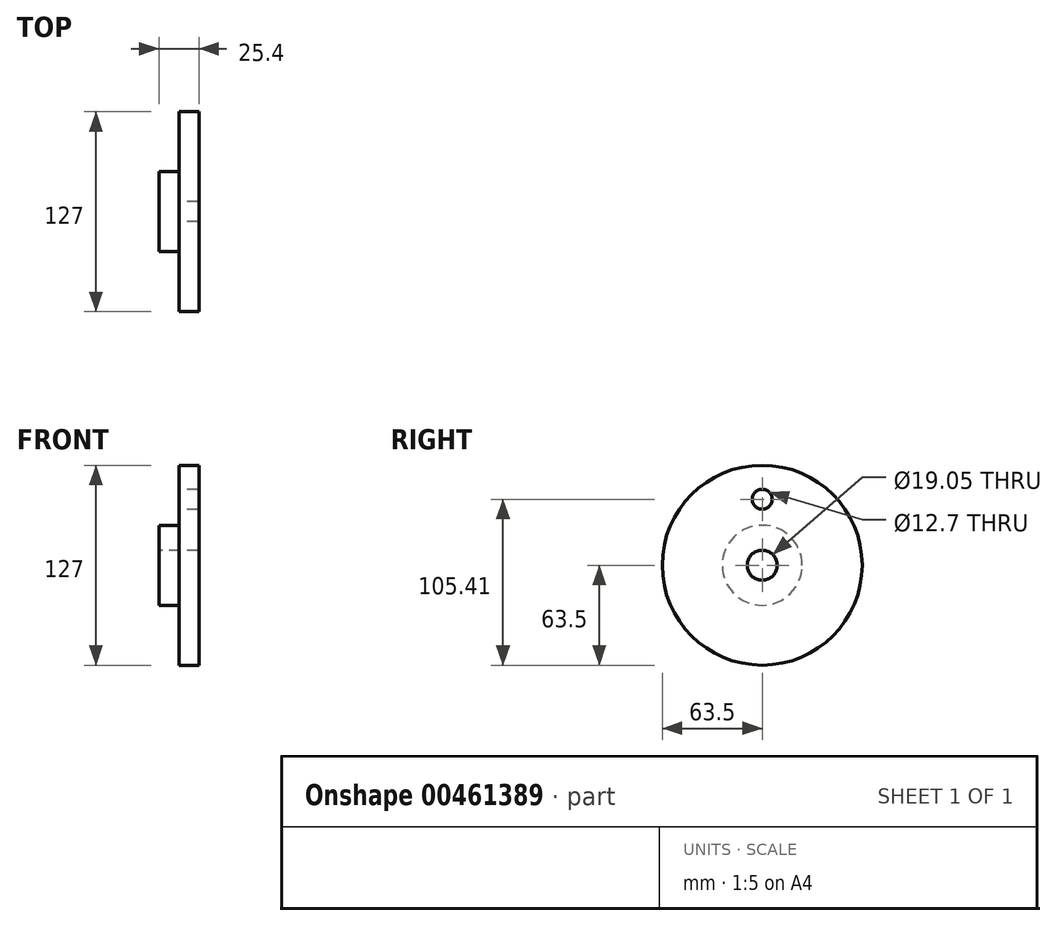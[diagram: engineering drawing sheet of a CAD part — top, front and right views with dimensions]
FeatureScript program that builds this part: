
annotation { "Feature Type Name" : "Feature", "Feature Type Description" : "" }
export const myFeature = defineFeature(function(context is Context, id is Id, definition is map)
    precondition{}
    {
        {
            var Q0;
            Q0=qCreatedBy(makeId("Front.planeOp"),FACE);
            var sketch = newSketch(context, id + "F0", { "sketchPlane" : qUnion([Q0])});
            skLineSegment(sketch, "E0", {"start": v(0, 0) * mm, "end": v(12.7, 0) * mm});
            skLineSegment(sketch, "E1", {"start": v(12.7, 0) * mm, "end": v(12.7, -53.98) * mm});
            skLineSegment(sketch, "E2", {"start": v(12.7, -53.98) * mm, "end": v(-12.7, -53.98) * mm});
            skLineSegment(sketch, "E3", {"start": v(-12.7, -53.98) * mm, "end": v(-12.7, -38.1) * mm});
            skLineSegment(sketch, "E4", {"start": v(-12.7, -38.1) * mm, "end": v(0, -38.1) * mm});
            skLineSegment(sketch, "E5", {"start": v(0, -38.1) * mm, "end": v(0, 0) * mm});
            skLineSegment(sketch, "E6", {"start": v(-48.6, -63.5) * mm, "end": v(129.62, -63.5) * mm, "construction": true});
            skSolve(sketch);
        }
        {
            var Q0;
            Q0=makeQuery(id+"F0.imprint","IMPRINT",FACE,{"disambiguationData":[TD([[makeQuery(id+"F0.imprint","IMPRINT",EDGE,{"derivedFrom":sQuery(id+"F0.wireOp",EDGE,"E0")}),-1.0]])]});
            var Q1;
            Q1=sQuery(id+"F0.wireOp",EDGE,"E6");
            revolve(context, id + "F1", {"entities" : qUnion([Q0]), "axis" : qUnion([Q1]), "revolveType" : RevolveType.FULL});
        }
        {
            var Q0;
            Q0=makeQuery(id+"F1.opRevolve","SWEPT_FACE",FACE,{"disambiguationData":[OSD([sQuery(id+"F0.wireOp",EDGE,"E5")])]});
            var sketch = newSketch(context, id + "F2", { "sketchPlane" : qUnion([Q0])});
            skLineSegment(sketch, "E7", {"start": v(0, -63.5) * mm, "end": v(0, -21.59) * mm, "construction": true});
            skSolve(sketch);
        }
        {
            var Q0;
            Q0=sQuery(id+"F2.wireOp",VERTEX,"E7.end");
            var Q1;
            Q1=makeQuery(id+"F1.opRevolve","SWEPT_BODY",BODY,{"disambiguationData":[OSD([sQuery(id+"F0.wireOp",EDGE,"E0"),sQuery(id+"F0.wireOp",EDGE,"E1"),sQuery(id+"F0.wireOp",EDGE,"E2"),sQuery(id+"F0.wireOp",EDGE,"E3"),sQuery(id+"F0.wireOp",EDGE,"E4"),sQuery(id+"F0.wireOp",EDGE,"E5")])]});
            hole(context, id + "F3", {"style" : HoleStyle.SIMPLE, "endStyle" : HoleEndStyle.THROUGH, "holeDiameter" : 12.7 * mm, "isTappedThrough" : true, "tappedDepth" : 12.7 * mm, "tapClearance" : 3, "locations" : qUnion([Q0]), "scope" : qUnion([Q1])});
        }
    });
